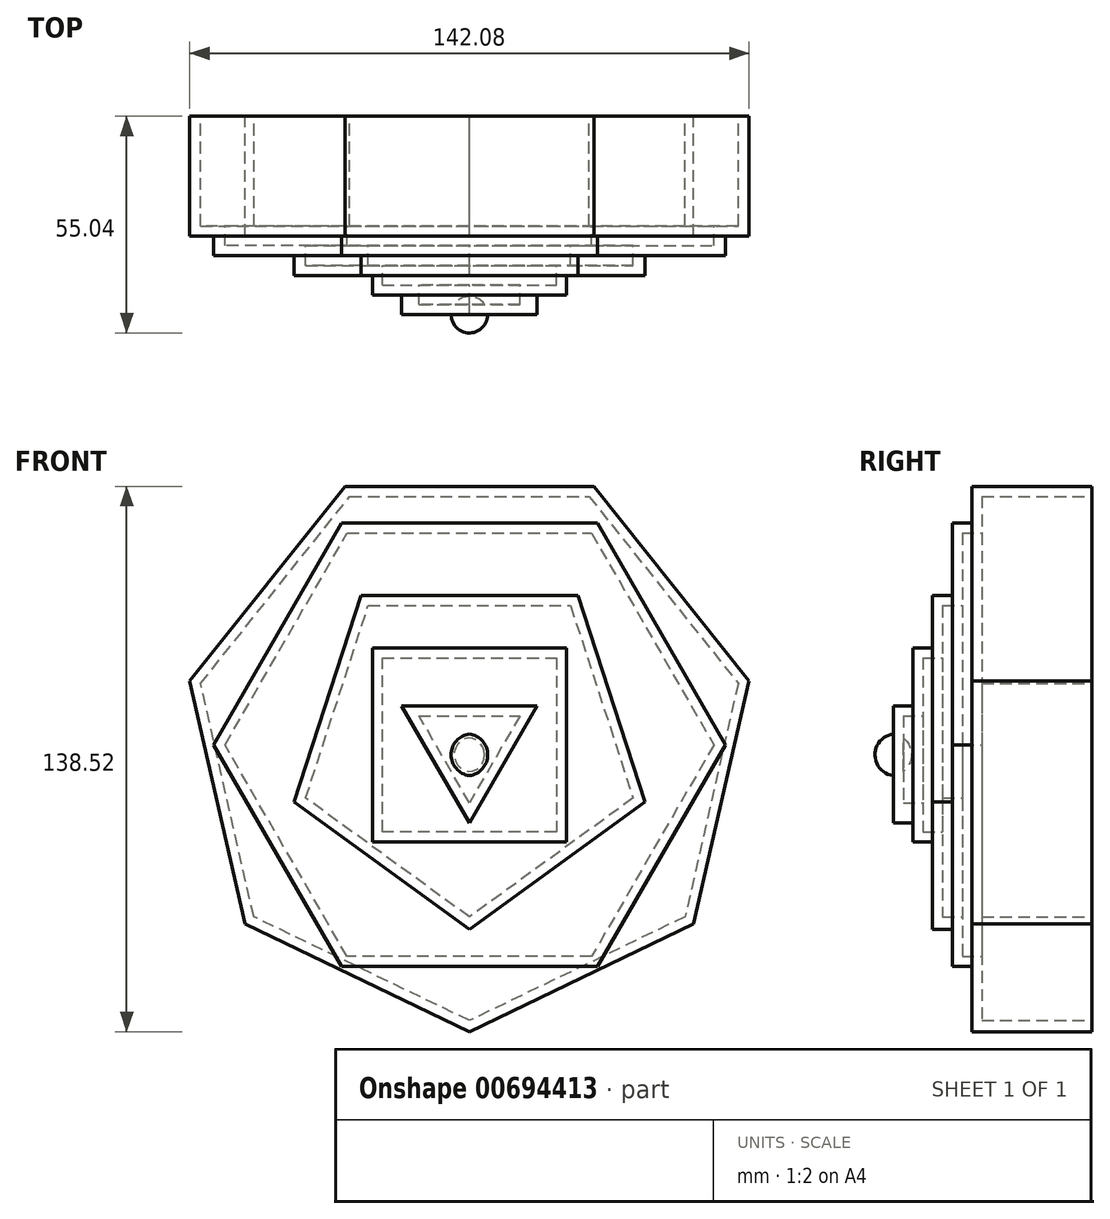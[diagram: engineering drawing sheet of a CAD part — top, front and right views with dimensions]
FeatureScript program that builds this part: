
annotation { "Feature Type Name" : "Feature", "Feature Type Description" : "" }
export const myFeature = defineFeature(function(context is Context, id is Id, definition is map)
    precondition{}
    {
        {
            var Q0;
            Q0=qCreatedBy(makeId("Front.planeOp"),FACE);
            var sketch = newSketch(context, id + "F0", { "sketchPlane" : qUnion([Q0])});
            skCircle(sketch, "E0.cCircle", {"center": v(0, 0) * mm, "radius": 65.65 * mm, "construction": true});
            skLineSegment(sketch, "E0.0", {"start": v(-31.62, 65.65) * mm, "end": v(31.62, 65.65) * mm});
            skLineSegment(sketch, "E0.1", {"start": v(31.62, 65.65) * mm, "end": v(71.04, 16.21) * mm});
            skLineSegment(sketch, "E0.2", {"start": v(71.04, 16.21) * mm, "end": v(56.97, -45.43) * mm});
            skLineSegment(sketch, "E0.3", {"start": v(56.97, -45.43) * mm, "end": v(0, -72.87) * mm});
            skLineSegment(sketch, "E0.4", {"start": v(0, -72.87) * mm, "end": v(-56.97, -45.43) * mm});
            skLineSegment(sketch, "E0.5", {"start": v(-56.97, -45.43) * mm, "end": v(-71.04, 16.21) * mm});
            skLineSegment(sketch, "E0.6", {"start": v(-71.04, 16.21) * mm, "end": v(-31.62, 65.65) * mm});
            skPoint(sketch, "E0.0.midPoint", {"position": v(0, 65.65) * mm});
            skSolve(sketch);
        }
        {
            var Q0;
            Q0 = qSketchRegion(id + "F0", true);
            extrude(context, id + "F1", {"entities" : qUnion([Q0]), "depth" : 5 * mm, "offsetDistance" : 25.4 * mm});
        }
        {
            var Q0;
            Q0=makeQuery(id+"F1.opExtrude","CAP_FACE",FACE,{"disambiguationData":[OSD([sQuery(id+"F0.wireOp",EDGE,"E0.0"),sQuery(id+"F0.wireOp",EDGE,"E0.1"),sQuery(id+"F0.wireOp",EDGE,"E0.2"),sQuery(id+"F0.wireOp",EDGE,"E0.3"),sQuery(id+"F0.wireOp",EDGE,"E0.4"),sQuery(id+"F0.wireOp",EDGE,"E0.5"),sQuery(id+"F0.wireOp",EDGE,"E0.6")])],"isStart":false});
            var sketch = newSketch(context, id + "F2", { "sketchPlane" : qUnion([Q0])});
            skCircle(sketch, "E1.cCircle", {"center": v(0, 0) * mm, "radius": 56.33 * mm, "construction": true});
            skLineSegment(sketch, "E1.0", {"start": v(-32.52, 56.33) * mm, "end": v(32.52, 56.33) * mm});
            skLineSegment(sketch, "E1.1", {"start": v(32.52, 56.33) * mm, "end": v(65.04, 0) * mm});
            skLineSegment(sketch, "E1.2", {"start": v(65.04, 0) * mm, "end": v(32.52, -56.33) * mm});
            skLineSegment(sketch, "E1.3", {"start": v(32.52, -56.33) * mm, "end": v(-32.52, -56.33) * mm});
            skLineSegment(sketch, "E1.4", {"start": v(-32.52, -56.33) * mm, "end": v(-65.04, 0) * mm});
            skLineSegment(sketch, "E1.5", {"start": v(-65.04, 0) * mm, "end": v(-32.52, 56.33) * mm});
            skPoint(sketch, "E1.0.midPoint", {"position": v(0, 56.33) * mm});
            skSolve(sketch);
        }
        {
            var Q0;
            Q0 = qSketchRegion(id + "F2", true);
            extrude(context, id + "F3", {"entities" : qUnion([Q0]), "operationType" : NewBodyOperationType.ADD, "depth" : 5 * mm, "offsetDistance" : 25.4 * mm});
        }
        {
            var Q0;
            Q0=makeQuery(id+"F3.opExtrude","CAP_FACE",FACE,{"disambiguationData":[OSD([sQuery(id+"F2.wireOp",EDGE,"E1.0"),sQuery(id+"F2.wireOp",EDGE,"E1.1"),sQuery(id+"F2.wireOp",EDGE,"E1.2"),sQuery(id+"F2.wireOp",EDGE,"E1.3"),sQuery(id+"F2.wireOp",EDGE,"E1.4"),sQuery(id+"F2.wireOp",EDGE,"E1.5")])],"isStart":false});
            var sketch = newSketch(context, id + "F4", { "sketchPlane" : qUnion([Q0])});
            skCircle(sketch, "E2.cCircle", {"center": v(0, 0) * mm, "radius": 37.92 * mm, "construction": true});
            skLineSegment(sketch, "E2.0", {"start": v(-27.55, 37.92) * mm, "end": v(27.55, 37.92) * mm});
            skLineSegment(sketch, "E2.1", {"start": v(27.55, 37.92) * mm, "end": v(44.58, -14.48) * mm});
            skLineSegment(sketch, "E2.2", {"start": v(44.58, -14.48) * mm, "end": v(0, -46.87) * mm});
            skLineSegment(sketch, "E2.3", {"start": v(0, -46.87) * mm, "end": v(-44.58, -14.48) * mm});
            skLineSegment(sketch, "E2.4", {"start": v(-44.58, -14.48) * mm, "end": v(-27.55, 37.92) * mm});
            skPoint(sketch, "E2.0.midPoint", {"position": v(0, 37.92) * mm});
            skSolve(sketch);
        }
        {
            var Q0;
            Q0 = qSketchRegion(id + "F4", true);
            extrude(context, id + "F5", {"entities" : qUnion([Q0]), "operationType" : NewBodyOperationType.ADD, "depth" : 5 * mm, "offsetDistance" : 25.4 * mm});
        }
        {
            var Q0;
            Q0=makeQuery(id+"F5.opExtrude","CAP_FACE",FACE,{"disambiguationData":[OSD([sQuery(id+"F4.wireOp",EDGE,"E2.0"),sQuery(id+"F4.wireOp",EDGE,"E2.1"),sQuery(id+"F4.wireOp",EDGE,"E2.2"),sQuery(id+"F4.wireOp",EDGE,"E2.3"),sQuery(id+"F4.wireOp",EDGE,"E2.4")])],"isStart":false});
            var sketch = newSketch(context, id + "F6", { "sketchPlane" : qUnion([Q0])});
            skCircle(sketch, "E3.cCircle", {"center": v(0, 0) * mm, "radius": 24.67 * mm, "construction": true});
            skLineSegment(sketch, "E3.0", {"start": v(-24.67, 24.67) * mm, "end": v(24.67, 24.67) * mm});
            skLineSegment(sketch, "E3.1", {"start": v(24.67, 24.67) * mm, "end": v(24.67, -24.67) * mm});
            skLineSegment(sketch, "E3.2", {"start": v(24.67, -24.67) * mm, "end": v(-24.67, -24.67) * mm});
            skLineSegment(sketch, "E3.3", {"start": v(-24.67, -24.67) * mm, "end": v(-24.67, 24.67) * mm});
            skPoint(sketch, "E3.0.midPoint", {"position": v(0, 24.67) * mm});
            skSolve(sketch);
        }
        {
            var Q0;
            Q0 = qSketchRegion(id + "F6", true);
            extrude(context, id + "F7", {"entities" : qUnion([Q0]), "operationType" : NewBodyOperationType.ADD, "depth" : 5 * mm, "offsetDistance" : 25.4 * mm});
        }
        {
            var Q0;
            Q0=makeQuery(id+"F7.opExtrude","CAP_FACE",FACE,{"disambiguationData":[OSD([sQuery(id+"F6.wireOp",EDGE,"E3.0"),sQuery(id+"F6.wireOp",EDGE,"E3.1"),sQuery(id+"F6.wireOp",EDGE,"E3.2"),sQuery(id+"F6.wireOp",EDGE,"E3.3")])],"isStart":false});
            var sketch = newSketch(context, id + "F8", { "sketchPlane" : qUnion([Q0])});
            skCircle(sketch, "E4.cCircle", {"center": v(0, 0) * mm, "radius": 9.94 * mm, "construction": true});
            skLineSegment(sketch, "E4.0", {"start": v(-17.22, 9.94) * mm, "end": v(17.22, 9.94) * mm});
            skLineSegment(sketch, "E4.1", {"start": v(17.22, 9.94) * mm, "end": v(0, -19.88) * mm});
            skLineSegment(sketch, "E4.2", {"start": v(0, -19.88) * mm, "end": v(-17.22, 9.94) * mm});
            skPoint(sketch, "E4.0.midPoint", {"position": v(0, 9.94) * mm});
            skSolve(sketch);
        }
        {
            var Q0;
            Q0 = qSketchRegion(id + "F8", true);
            extrude(context, id + "F9", {"entities" : qUnion([Q0]), "operationType" : NewBodyOperationType.ADD, "depth" : 5 * mm, "offsetDistance" : 25.4 * mm});
        }
        {
            var Q0;
            Q0=makeQuery(id+"F1.opExtrude","CAP_FACE",FACE,{"disambiguationData":[OSD([sQuery(id+"F0.wireOp",EDGE,"E0.0"),sQuery(id+"F0.wireOp",EDGE,"E0.1"),sQuery(id+"F0.wireOp",EDGE,"E0.2"),sQuery(id+"F0.wireOp",EDGE,"E0.3"),sQuery(id+"F0.wireOp",EDGE,"E0.4"),sQuery(id+"F0.wireOp",EDGE,"E0.5"),sQuery(id+"F0.wireOp",EDGE,"E0.6")])],"isStart":true});
            shell(context, id + "F10", {"entities" : qUnion([Q0]), "thickness" : 2.54 * mm});
        }
        {
            var Q0;
            Q0=makeQuery(id+"F9.opExtrude","CAP_FACE",FACE,{"disambiguationData":[OSD([sQuery(id+"F8.wireOp",EDGE,"E4.0"),sQuery(id+"F8.wireOp",EDGE,"E4.1"),sQuery(id+"F8.wireOp",EDGE,"E4.2")])],"isStart":false});
            var sketch = newSketch(context, id + "F11", { "sketchPlane" : qUnion([Q0])});
            skArc(sketch, "E5", {"start": v(0, 2.78) * mm, "mid": v(-4.64, -2.52) * mm, "end": v(0, -7.81) * mm});
            skLineSegment(sketch, "E6", {"start": v(0, 2.78) * mm, "end": v(0, -7.81) * mm});
            skSolve(sketch);
        }
        {
            var Q0;
            Q0 = qSketchRegion(id + "F11", true);
            var Q1;
            Q1=sQuery(id+"F11.wireOp",EDGE,"E6");
            revolve(context, id + "F12", {"operationType" : NewBodyOperationType.ADD, "entities" : qUnion([Q0]), "axis" : qUnion([Q1]), "revolveType" : RevolveType.FULL});
        }
        {
            var Q0;
            Q0=makeQuery(id+"F1.opExtrude","CAP_FACE",FACE,{"disambiguationData":[OSD([sQuery(id+"F0.wireOp",EDGE,"E0.0"),sQuery(id+"F0.wireOp",EDGE,"E0.1"),sQuery(id+"F0.wireOp",EDGE,"E0.2"),sQuery(id+"F0.wireOp",EDGE,"E0.3"),sQuery(id+"F0.wireOp",EDGE,"E0.4"),sQuery(id+"F0.wireOp",EDGE,"E0.5"),sQuery(id+"F0.wireOp",EDGE,"E0.6")])],"isStart":true});
            extrude(context, id + "F13", {"entities" : qUnion([Q0]), "operationType" : NewBodyOperationType.ADD, "depth" : 25.4 * mm, "offsetDistance" : 25.4 * mm});
        }
    });
